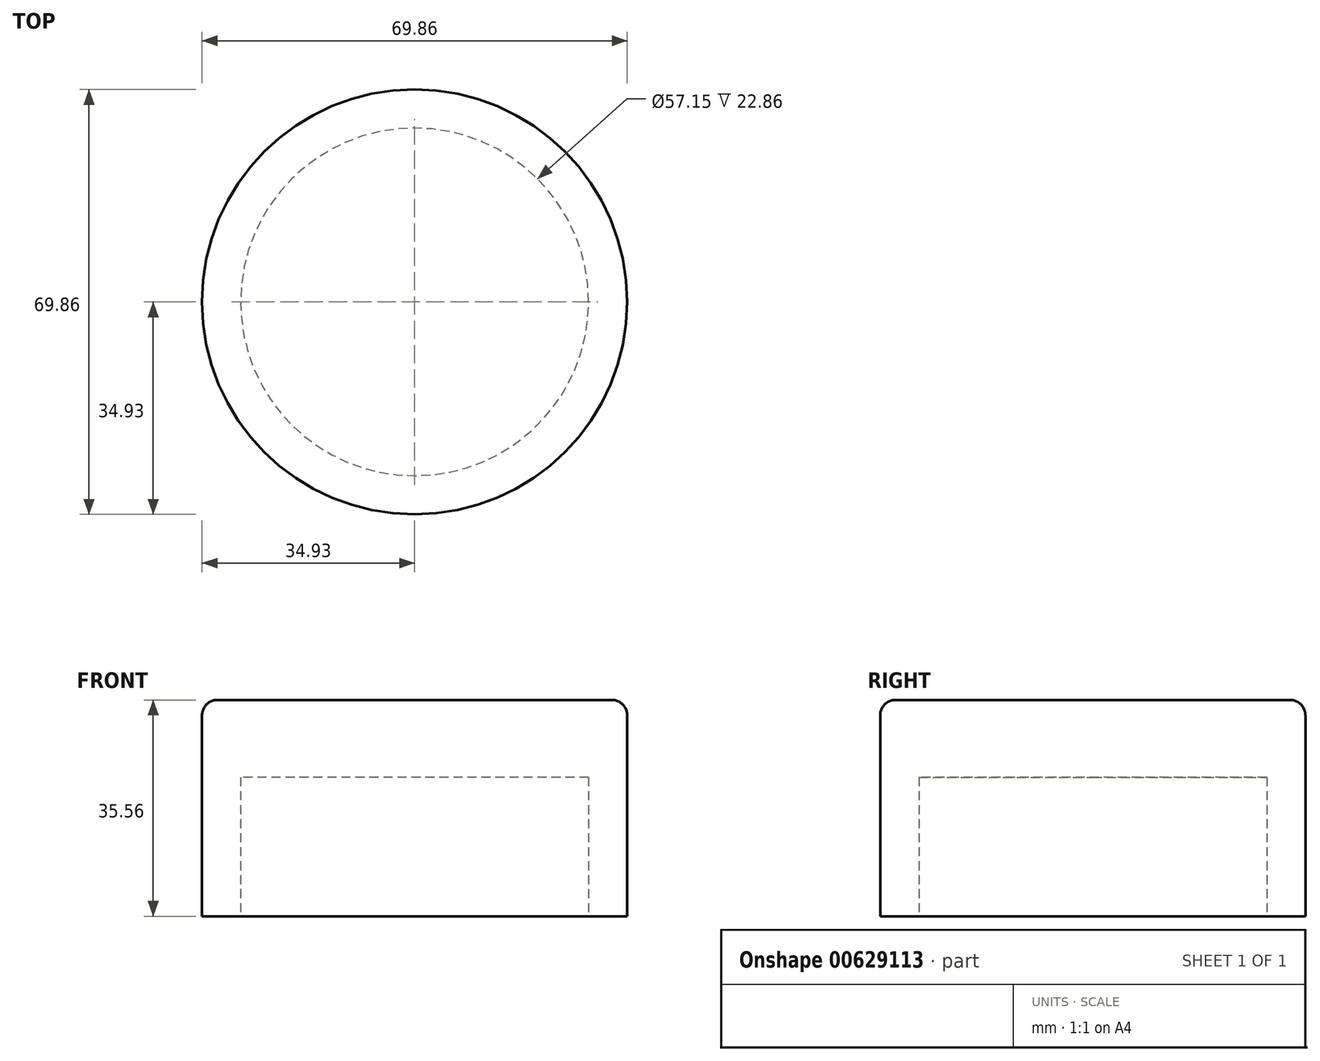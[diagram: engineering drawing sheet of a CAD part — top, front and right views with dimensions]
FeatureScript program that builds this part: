
annotation { "Feature Type Name" : "Feature", "Feature Type Description" : "" }
export const myFeature = defineFeature(function(context is Context, id is Id, definition is map)
    precondition{}
    {
        {
            var Q0;
            Q0=qCreatedBy(makeId("Top.planeOp"),FACE);
            var sketch = newSketch(context, id + "F0", { "sketchPlane" : qUnion([Q0])});
            skCircle(sketch, "E0", {"center": v(0, 0) * mm, "radius": 34.93 * mm});
            skSolve(sketch);
        }
        {
            var Q0;
            Q0=makeQuery(id+"F0.imprint","IMPRINT",FACE,{"disambiguationData":[TD([[makeQuery(id+"F0.imprint","IMPRINT",EDGE,{"derivedFrom":sQuery(id+"F0.wireOp",EDGE,"E0")}),1.0]])]});
            var sketch = newSketch(context, id + "F1", { "sketchPlane" : qUnion([Q0])});
            skSolve(sketch);
        }
        {
            var Q0;
            Q0=makeQuery(id+"F1.imprint","IMPRINT",FACE,{"disambiguationData":[TD([[makeQuery(id+"F1.imprint","IMPRINT",EDGE,{"derivedFrom":makeQuery(id+"F0.imprint","IMPRINT",EDGE,{"derivedFrom":sQuery(id+"F0.wireOp",EDGE,"E0")})}),1.0]])]});
            extrude(context, id + "F2", {"entities" : qUnion([Q0]), "depth" : 35.56 * mm, "offsetDistance" : 25.4 * mm});
        }
        {
            var Q0;
            Q0=makeQuery(id+"F2.opExtrude","CAP_EDGE",EDGE,{"disambiguationData":[OSD([sQuery(id+"F0.wireOp",EDGE,"E0")])],"isStart":false});
            fillet(context, id + "F3", {"entities" : qUnion([Q0]), "radius" : 2.54 * mm, "tangentPropagation" : true, "allowEdgeOverflow" : false});
        }
        {
            var Q0;
            Q0=qCreatedBy(makeId("Top.planeOp"),FACE);
            var sketch = newSketch(context, id + "F4", { "sketchPlane" : qUnion([Q0])});
            skCircle(sketch, "E1", {"center": v(0, 0) * mm, "radius": 28.58 * mm});
            skSolve(sketch);
        }
        {
            var Q0;
            Q0=makeQuery(id+"F4.imprint","IMPRINT",FACE,{"disambiguationData":[TD([[makeQuery(id+"F4.imprint","IMPRINT",EDGE,{"derivedFrom":sQuery(id+"F4.wireOp",EDGE,"E1")}),1.0]])]});
            var Q1;
            Q1=sQuery(id+"F4.wireOp",EDGE,"E1");
            extrude(context, id + "F5", {"entities" : qUnion([Q0]), "operationType" : NewBodyOperationType.REMOVE, "surfaceEntities" : qUnion([Q1]), "depth" : 22.86 * mm, "offsetDistance" : 25.4 * mm});
        }
    });
